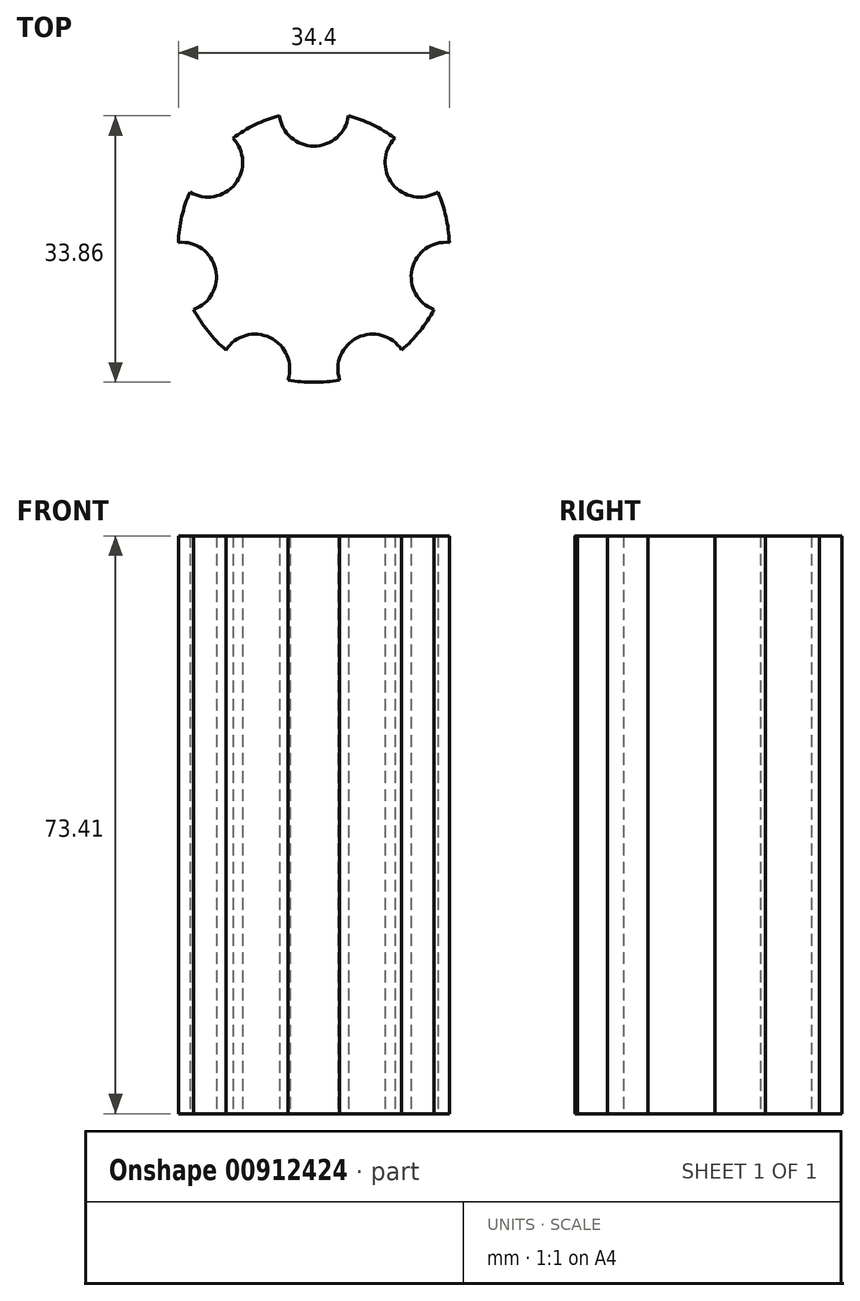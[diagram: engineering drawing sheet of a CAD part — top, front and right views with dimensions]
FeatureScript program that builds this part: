
annotation { "Feature Type Name" : "Feature", "Feature Type Description" : "" }
export const myFeature = defineFeature(function(context is Context, id is Id, definition is map)
    precondition{}
    {
        {
            var Q0;
            Q0=qCreatedBy(makeId("Top.planeOp"),FACE);
            var sketch = newSketch(context, id + "F0", { "sketchPlane" : qUnion([Q0])});
            skArc(sketch, "E0", {"start": v(-15.74, 6.96) * mm, "mid": v(-16.78, 3.83) * mm, "end": v(-17.2, 0.56) * mm});
            skArc(sketch, "E1", {"start": v(-4.38, 16.65) * mm, "mid": v(0, 12.8) * mm, "end": v(4.38, 16.65) * mm});
            skArc(sketch, "E2.1.0", {"start": v(-15.74, 6.96) * mm, "mid": v(-10, 7.98) * mm, "end": v(-10.29, 13.8) * mm});
            skArc(sketch, "E2.2.0", {"start": v(-15.26, -7.97) * mm, "mid": v(-12.48, -2.85) * mm, "end": v(-17.2, 0.56) * mm});
            skArc(sketch, "E2.3.0", {"start": v(-3.28, -16.9) * mm, "mid": v(-5.55, -11.53) * mm, "end": v(-11.16, -13.1) * mm});
            skArc(sketch, "E2.4.0", {"start": v(11.16, -13.1) * mm, "mid": v(5.55, -11.53) * mm, "end": v(3.28, -16.9) * mm});
            skArc(sketch, "E2.5.0", {"start": v(17.2, 0.56) * mm, "mid": v(12.48, -2.85) * mm, "end": v(15.26, -7.97) * mm});
            skArc(sketch, "E2.6.0", {"start": v(10.29, 13.8) * mm, "mid": v(10, 7.98) * mm, "end": v(15.74, 6.96) * mm});
            skArc(sketch, "E3.trimOffspring", {"start": v(-15.26, -7.97) * mm, "mid": v(-13.46, -10.73) * mm, "end": v(-11.16, -13.1) * mm});
            skArc(sketch, "E4.trimOffspring", {"start": v(-3.28, -16.9) * mm, "mid": v(0, -17.21) * mm, "end": v(3.28, -16.9) * mm});
            skArc(sketch, "E5.trimOffspring", {"start": v(11.16, -13.1) * mm, "mid": v(13.46, -10.73) * mm, "end": v(15.26, -7.97) * mm});
            skArc(sketch, "E6.trimOffspring", {"start": v(17.2, 0.56) * mm, "mid": v(16.78, 3.83) * mm, "end": v(15.74, 6.96) * mm});
            skArc(sketch, "E7.trimOffspring", {"start": v(10.29, 13.8) * mm, "mid": v(7.47, 15.5) * mm, "end": v(4.38, 16.65) * mm});
            skArc(sketch, "E8.trimOffspring", {"start": v(-4.38, 16.65) * mm, "mid": v(-7.47, 15.5) * mm, "end": v(-10.29, 13.8) * mm});
            skSolve(sketch);
        }
        {
            var Q0;
            Q0 = qSketchRegion(id + "F0", true);
            extrude(context, id + "F1", {"entities" : qUnion([Q0]), "depth" : 73.4 * mm, "offsetDistance" : 25.4 * mm});
        }
    });
